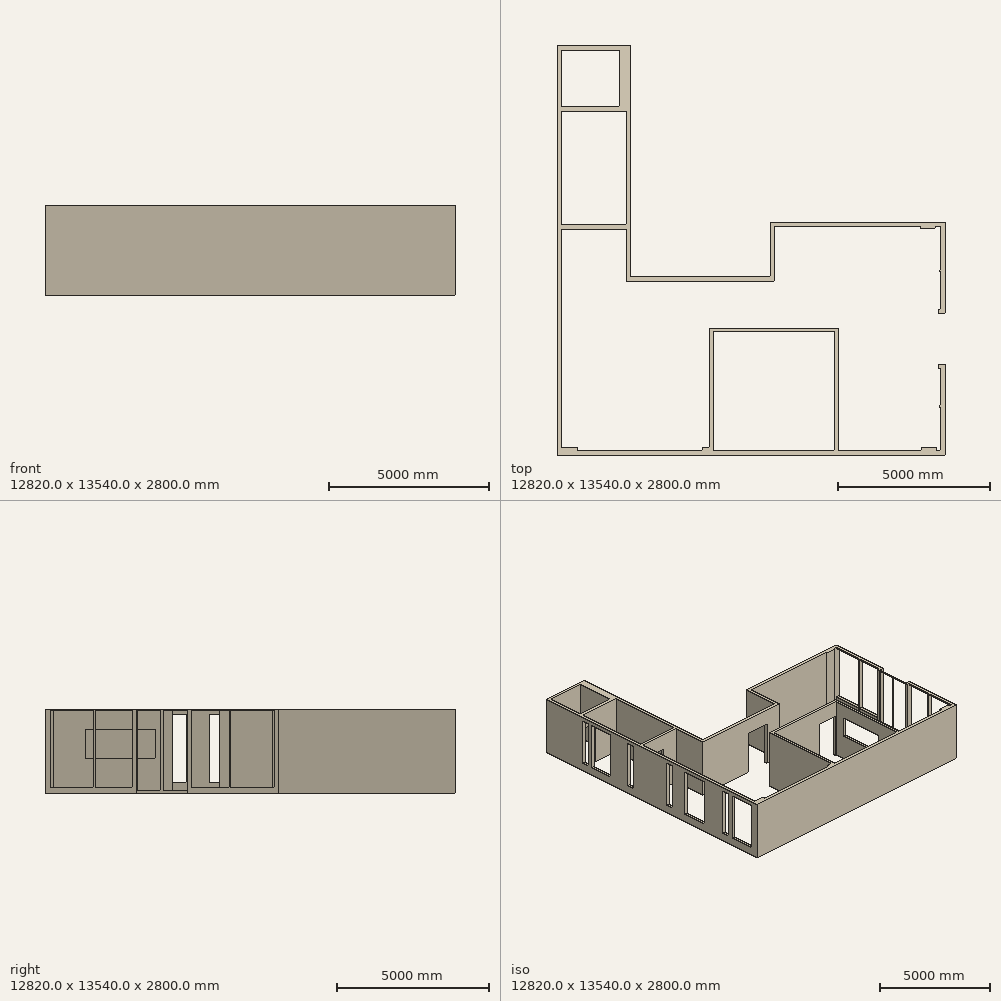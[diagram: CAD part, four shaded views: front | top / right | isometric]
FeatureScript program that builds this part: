
annotation { "Feature Type Name" : "Feature", "Feature Type Description" : "" }
export const myFeature = defineFeature(function(context is Context, id is Id, definition is map)
    precondition{}
    {
        {
            var Q0;
            Q0=qCreatedBy(makeId("Top.planeOp"),FACE);
            var sketch = newSketch(context, id + "F0", { "sketchPlane" : qUnion([Q0])});
            skLineSegment(sketch, "E0", {"start": v(0, 13240) * mm, "end": v(1900, 13240) * mm});
            skLineSegment(sketch, "E1", {"start": v(2130, 11200) * mm, "end": v(2130, 5610) * mm});
            skLineSegment(sketch, "E2", {"start": v(2130, 5610) * mm, "end": v(7030, 5610) * mm});
            skLineSegment(sketch, "E3", {"start": v(7030, 5610) * mm, "end": v(7030, 7400) * mm});
            skLineSegment(sketch, "E4", {"start": v(7030, 7400) * mm, "end": v(11840, 7400) * mm});
            skLineSegment(sketch, "E5", {"start": v(12500, 7400) * mm, "end": v(12500, 5970) * mm});
            skLineSegment(sketch, "E6", {"start": v(12500, 0) * mm, "end": v(12360, 0) * mm});
            skLineSegment(sketch, "E7", {"start": v(0, 125) * mm, "end": v(0, 11200) * mm});
            skLineSegment(sketch, "E8", {"start": v(-150, 13390) * mm, "end": v(-150, -150) * mm});
            skLineSegment(sketch, "E9", {"start": v(-150, -150) * mm, "end": v(12670, -150) * mm});
            skLineSegment(sketch, "E10", {"start": v(12670, -150) * mm, "end": v(12670, 2865) * mm});
            skLineSegment(sketch, "E11", {"start": v(12670, 7550) * mm, "end": v(6880, 7550) * mm});
            skLineSegment(sketch, "E12", {"start": v(2280, 13390) * mm, "end": v(-150, 13390) * mm});
            skLineSegment(sketch, "E13", {"start": v(2130, 11200) * mm, "end": v(0, 11200) * mm});
            skLineSegment(sketch, "E14", {"start": v(0, 11360) * mm, "end": v(1900, 11360) * mm});
            skLineSegment(sketch, "E15", {"start": v(1900, 11360) * mm, "end": v(1900, 13240) * mm});
            skLineSegment(sketch, "E16", {"start": v(0, 125) * mm, "end": v(500, 125) * mm});
            skLineSegment(sketch, "E17", {"start": v(500, 125) * mm, "end": v(500, 0) * mm});
            skLineSegment(sketch, "E18", {"start": v(4630, 0) * mm, "end": v(4630, 110) * mm});
            skLineSegment(sketch, "E19", {"start": v(4630, 110) * mm, "end": v(5010, 110) * mm});
            skLineSegment(sketch, "E20", {"start": v(5010, 110) * mm, "end": v(5010, 0) * mm});
            skLineSegment(sketch, "E21.trimOffspring", {"start": v(4630, 0) * mm, "end": v(500, 0) * mm});
            skLineSegment(sketch, "E22", {"start": v(2280, 5760) * mm, "end": v(2280, 13390) * mm});
            skLineSegment(sketch, "E23", {"start": v(2280, 5760) * mm, "end": v(6880, 5760) * mm});
            skLineSegment(sketch, "E24", {"start": v(6880, 5760) * mm, "end": v(6880, 7550) * mm});
            skLineSegment(sketch, "E25.top", {"start": v(11840, 7350) * mm, "end": v(12340, 7350) * mm});
            skLineSegment(sketch, "E25.left", {"start": v(11840, 7400) * mm, "end": v(11840, 7350) * mm});
            skLineSegment(sketch, "E25.right", {"start": v(12340, 7400) * mm, "end": v(12340, 7350) * mm});
            skLineSegment(sketch, "E26.trimOffspring", {"start": v(12340, 7400) * mm, "end": v(12500, 7400) * mm});
            skLineSegment(sketch, "E27.top", {"start": v(11860, 110) * mm, "end": v(12360, 110) * mm});
            skLineSegment(sketch, "E27.left", {"start": v(11860, 0) * mm, "end": v(11860, 110) * mm});
            skLineSegment(sketch, "E27.right", {"start": v(12360, 0) * mm, "end": v(12360, 110) * mm});
            skLineSegment(sketch, "E28.trimOffspring", {"start": v(11860, 0) * mm, "end": v(5010, 0) * mm});
            skLineSegment(sketch, "E29.trimOffspring", {"start": v(0, 11360) * mm, "end": v(0, 13240) * mm});
            skLineSegment(sketch, "E30", {"start": v(12500, 5970) * mm, "end": v(12470, 5970) * mm});
            skLineSegment(sketch, "E31", {"start": v(12470, 5970) * mm, "end": v(12470, 5910) * mm});
            skLineSegment(sketch, "E32", {"start": v(12470, 5910) * mm, "end": v(12500, 5910) * mm});
            skLineSegment(sketch, "E33.trimOffspring", {"start": v(12500, 5910) * mm, "end": v(12500, 4670) * mm});
            skLineSegment(sketch, "E34", {"start": v(12500, 1430) * mm, "end": v(12470, 1430) * mm});
            skLineSegment(sketch, "E35", {"start": v(12470, 1430) * mm, "end": v(12470, 1490) * mm});
            skLineSegment(sketch, "E36", {"start": v(12470, 1490) * mm, "end": v(12500, 1490) * mm});
            skLineSegment(sketch, "E37.trimOffspring", {"start": v(12500, 1430) * mm, "end": v(12500, 0) * mm});
            skLineSegment(sketch, "E38", {"start": v(12500, 4670) * mm, "end": v(12420, 4670) * mm});
            skLineSegment(sketch, "E39", {"start": v(12420, 4670) * mm, "end": v(12420, 2730) * mm});
            skLineSegment(sketch, "E40", {"start": v(12420, 2730) * mm, "end": v(12500, 2730) * mm});
            skLineSegment(sketch, "E41.trimOffspring", {"start": v(12500, 2730) * mm, "end": v(12500, 1490) * mm});
            skLineSegment(sketch, "E42", {"start": v(12670, 4535) * mm, "end": v(12440, 4535) * mm});
            skLineSegment(sketch, "E43", {"start": v(12440, 4535) * mm, "end": v(12440, 2865) * mm});
            skLineSegment(sketch, "E44", {"start": v(12440, 2865) * mm, "end": v(12670, 2865) * mm});
            skLineSegment(sketch, "E45.trimOffspring", {"start": v(12670, 4535) * mm, "end": v(12670, 7550) * mm});
            skSolve(sketch);
        }
        {
            var Q0;
            Q0 = qSketchRegion(id + "F0", true);
            extrude(context, id + "F1", {"entities" : qUnion([Q0]), "depth" : 2800 * mm, "offsetDistance" : 25 * mm});
        }
        {
            var Q0;
            Q0=makeQuery(id+"F1.opExtrude","SWEPT_FACE",FACE,{"disambiguationData":[OSD([sQuery(id+"F0.wireOp",EDGE,"E13")])]});
            var sketch = newSketch(context, id + "F2", { "sketchPlane" : qUnion([Q0])});
            skLineSegment(sketch, "E46.bottom", {"start": v(70, 0) * mm, "end": v(840, 0) * mm});
            skLineSegment(sketch, "E46.top", {"start": v(70, 2050) * mm, "end": v(840, 2050) * mm});
            skLineSegment(sketch, "E46.left", {"start": v(70, 0) * mm, "end": v(70, 2050) * mm});
            skLineSegment(sketch, "E46.right", {"start": v(840, 0) * mm, "end": v(840, 2050) * mm});
            skSolve(sketch);
        }
        {
            var Q0;
            Q0=makeQuery(id+"F2.imprint","IMPRINT",FACE,{"disambiguationData":[TD([[makeQuery(id+"F2.imprint","IMPRINT",EDGE,{"derivedFrom":sQuery(id+"F2.wireOp",EDGE,"E46.bottom")}),-1.0]])]});
            extrude(context, id + "F3", {"entities" : qUnion([Q0]), "operationType" : NewBodyOperationType.REMOVE, "endBound" : BoundingType.UP_TO_NEXT, "oppositeDirection" : true, "depth" : 25 * mm, "offsetDistance" : 25 * mm});
        }
        {
            var Q0;
            Q0=makeQuery(id+"F1.opExtrude","SWEPT_FACE",FACE,{"disambiguationData":[OSD([sQuery(id+"F0.wireOp",EDGE,"E13")])]});
            cPlane(context, id + "F4", {"entities" : qUnion([Q0]), "cplaneType" : CPlaneType.OFFSET, "offset" : 3730 * mm, "width" : 150 * mm, "height" : 150 * mm});
        }
        {
            var Q0;
            Q0=qCreatedBy(id+"F4.planeOp",FACE);
            var sketch = newSketch(context, id + "F5", { "sketchPlane" : qUnion([Q0])});
            skLineSegment(sketch, "E47.bottom", {"start": v(0, 0) * mm, "end": v(560, 0) * mm});
            skLineSegment(sketch, "E47.top", {"start": v(0, 2800) * mm, "end": v(2130, 2800) * mm});
            skLineSegment(sketch, "E47.left", {"start": v(0, 0) * mm, "end": v(0, 2800) * mm});
            skLineSegment(sketch, "E47.right", {"start": v(2130, 0) * mm, "end": v(2130, 2800) * mm});
            skLineSegment(sketch, "E48.top", {"start": v(560, 2050) * mm, "end": v(1330, 2050) * mm});
            skLineSegment(sketch, "E48.left", {"start": v(560, 0) * mm, "end": v(560, 2050) * mm});
            skLineSegment(sketch, "E48.right", {"start": v(1330, 0) * mm, "end": v(1330, 2050) * mm});
            skLineSegment(sketch, "E49.trimOffspring", {"start": v(1330, 0) * mm, "end": v(2130, 0) * mm});
            skSolve(sketch);
        }
        {
            var Q0;
            Q0=makeQuery(id+"F5.imprint","IMPRINT",FACE,{"disambiguationData":[TD([[makeQuery(id+"F5.imprint","IMPRINT",EDGE,{"derivedFrom":sQuery(id+"F5.wireOp",EDGE,"E47.bottom")}),1.0]])]});
            extrude(context, id + "F6", {"entities" : qUnion([Q0]), "operationType" : NewBodyOperationType.ADD, "depth" : 150 * mm, "offsetDistance" : 25 * mm});
        }
        {
            var Q0;
            Q0=makeQuery(id+"F1.opExtrude","SWEPT_FACE",FACE,{"disambiguationData":[OSD([sQuery(id+"F0.wireOp",EDGE,"E2")])]});
            var sketch = newSketch(context, id + "F7", { "sketchPlane" : qUnion([Q0])});
            skLineSegment(sketch, "E50.bottom", {"start": v(6250, 0) * mm, "end": v(5070, 0) * mm});
            skLineSegment(sketch, "E50.top", {"start": v(6250, 2050) * mm, "end": v(5070, 2050) * mm});
            skLineSegment(sketch, "E50.left", {"start": v(6250, 0) * mm, "end": v(6250, 2050) * mm});
            skLineSegment(sketch, "E50.right", {"start": v(5070, 0) * mm, "end": v(5070, 2050) * mm});
            skSolve(sketch);
        }
        {
            var Q0;
            Q0=makeQuery(id+"F7.imprint","IMPRINT",FACE,{"disambiguationData":[TD([[makeQuery(id+"F7.imprint","IMPRINT",EDGE,{"derivedFrom":sQuery(id+"F7.wireOp",EDGE,"E50.bottom")}),1.0]])]});
            extrude(context, id + "F8", {"entities" : qUnion([Q0]), "operationType" : NewBodyOperationType.REMOVE, "endBound" : BoundingType.UP_TO_NEXT, "oppositeDirection" : true, "depth" : 25 * mm, "offsetDistance" : 25 * mm});
        }
        {
            var Q0;
            Q0=makeQuery(id+"F1.opExtrude","SWEPT_FACE",FACE,{"disambiguationData":[OSD([sQuery(id+"F0.wireOp",EDGE,"E8")])]});
            var sketch = newSketch(context, id + "F9", { "sketchPlane" : qUnion([Q0])});
            skLineSegment(sketch, "E51.bottom", {"start": v(-240, 390) * mm, "end": v(-1460, 390) * mm});
            skLineSegment(sketch, "E51.top", {"start": v(-240, 2610) * mm, "end": v(-1460, 2610) * mm});
            skLineSegment(sketch, "E51.left", {"start": v(-240, 390) * mm, "end": v(-240, 2610) * mm});
            skLineSegment(sketch, "E51.right", {"start": v(-1460, 390) * mm, "end": v(-1460, 2610) * mm});
            skLineSegment(sketch, "E52.bottom", {"start": v(-1660, 2610) * mm, "end": v(-2050, 2610) * mm});
            skLineSegment(sketch, "E52.top", {"start": v(-1660, 390) * mm, "end": v(-2050, 390) * mm});
            skLineSegment(sketch, "E52.left", {"start": v(-1660, 2610) * mm, "end": v(-1660, 390) * mm});
            skLineSegment(sketch, "E52.right", {"start": v(-2050, 2610) * mm, "end": v(-2050, 390) * mm});
            skLineSegment(sketch, "E53.bottom", {"start": v(-3240, 390) * mm, "end": v(-4500, 390) * mm});
            skLineSegment(sketch, "E53.top", {"start": v(-3240, 2610) * mm, "end": v(-4500, 2610) * mm});
            skLineSegment(sketch, "E53.left", {"start": v(-3240, 390) * mm, "end": v(-3240, 2610) * mm});
            skLineSegment(sketch, "E53.right", {"start": v(-4500, 390) * mm, "end": v(-4500, 2610) * mm});
            skLineSegment(sketch, "E54.bottom", {"start": v(-5270, 2610) * mm, "end": v(-5660, 2610) * mm});
            skLineSegment(sketch, "E54.top", {"start": v(-5270, 390) * mm, "end": v(-5660, 390) * mm});
            skLineSegment(sketch, "E54.left", {"start": v(-5270, 2610) * mm, "end": v(-5270, 390) * mm});
            skLineSegment(sketch, "E54.right", {"start": v(-5660, 2610) * mm, "end": v(-5660, 390) * mm});
            skLineSegment(sketch, "E55.bottom", {"start": v(-7780, 390) * mm, "end": v(-8170, 390) * mm});
            skLineSegment(sketch, "E55.top", {"start": v(-7780, 2610) * mm, "end": v(-8170, 2610) * mm});
            skLineSegment(sketch, "E55.left", {"start": v(-7780, 390) * mm, "end": v(-7780, 2610) * mm});
            skLineSegment(sketch, "E55.right", {"start": v(-8170, 390) * mm, "end": v(-8170, 2610) * mm});
            skLineSegment(sketch, "E56.bottom", {"start": v(-9250, 2610) * mm, "end": v(-10470, 2610) * mm});
            skLineSegment(sketch, "E56.top", {"start": v(-9250, 390) * mm, "end": v(-10470, 390) * mm});
            skLineSegment(sketch, "E56.left", {"start": v(-9250, 2610) * mm, "end": v(-9250, 390) * mm});
            skLineSegment(sketch, "E56.right", {"start": v(-10470, 2610) * mm, "end": v(-10470, 390) * mm});
            skLineSegment(sketch, "E57.bottom", {"start": v(-10670, 390) * mm, "end": v(-11060, 390) * mm});
            skLineSegment(sketch, "E57.top", {"start": v(-10670, 2610) * mm, "end": v(-11060, 2610) * mm});
            skLineSegment(sketch, "E57.left", {"start": v(-10670, 390) * mm, "end": v(-10670, 2610) * mm});
            skLineSegment(sketch, "E57.right", {"start": v(-11060, 390) * mm, "end": v(-11060, 2610) * mm});
            skSolve(sketch);
        }
        {
            var Q0;
            Q0=makeQuery(id+"F9.imprint","IMPRINT",FACE,{"disambiguationData":[TD([[makeQuery(id+"F9.imprint","IMPRINT",EDGE,{"derivedFrom":sQuery(id+"F9.wireOp",EDGE,"E54.bottom")}),1.0]])]});
            var Q1;
            Q1=makeQuery(id+"F9.imprint","IMPRINT",FACE,{"disambiguationData":[TD([[makeQuery(id+"F9.imprint","IMPRINT",EDGE,{"derivedFrom":sQuery(id+"F9.wireOp",EDGE,"E53.bottom")}),-1.0]])]});
            var Q2;
            Q2=makeQuery(id+"F9.imprint","IMPRINT",FACE,{"disambiguationData":[TD([[makeQuery(id+"F9.imprint","IMPRINT",EDGE,{"derivedFrom":sQuery(id+"F9.wireOp",EDGE,"E52.bottom")}),1.0]])]});
            var Q3;
            Q3=makeQuery(id+"F9.imprint","IMPRINT",FACE,{"disambiguationData":[TD([[makeQuery(id+"F9.imprint","IMPRINT",EDGE,{"derivedFrom":sQuery(id+"F9.wireOp",EDGE,"E51.bottom")}),-1.0]])]});
            var Q4;
            Q4=makeQuery(id+"F9.imprint","IMPRINT",FACE,{"disambiguationData":[TD([[makeQuery(id+"F9.imprint","IMPRINT",EDGE,{"derivedFrom":sQuery(id+"F9.wireOp",EDGE,"E55.bottom")}),-1.0]])]});
            var Q5;
            Q5=makeQuery(id+"F9.imprint","IMPRINT",FACE,{"disambiguationData":[TD([[makeQuery(id+"F9.imprint","IMPRINT",EDGE,{"derivedFrom":sQuery(id+"F9.wireOp",EDGE,"E56.bottom")}),1.0]])]});
            var Q6;
            Q6=makeQuery(id+"F9.imprint","IMPRINT",FACE,{"disambiguationData":[TD([[makeQuery(id+"F9.imprint","IMPRINT",EDGE,{"derivedFrom":sQuery(id+"F9.wireOp",EDGE,"E57.bottom")}),-1.0]])]});
            extrude(context, id + "F10", {"entities" : qUnion([Q0, Q1, Q2, Q3, Q4, Q5, Q6]), "operationType" : NewBodyOperationType.REMOVE, "endBound" : BoundingType.UP_TO_NEXT, "oppositeDirection" : true, "depth" : 25 * mm, "offsetDistance" : 25 * mm});
        }
        {
            var Q0;
            Q0=makeQuery(id+"F1.opExtrude","SWEPT_FACE",FACE,{"disambiguationData":[OSD([sQuery(id+"F0.wireOp",EDGE,"E10")])]});
            var sketch = newSketch(context, id + "F11", { "sketchPlane" : qUnion([Q0])});
            skLineSegment(sketch, "E58.bottom", {"start": v(2730, 200) * mm, "end": v(1490, 200) * mm});
            skLineSegment(sketch, "E58.top", {"start": v(2730, 2760) * mm, "end": v(1490, 2760) * mm});
            skLineSegment(sketch, "E58.left", {"start": v(2730, 200) * mm, "end": v(2730, 2760) * mm});
            skLineSegment(sketch, "E58.right", {"start": v(1490, 200) * mm, "end": v(1490, 2760) * mm});
            skLineSegment(sketch, "E59.bottom", {"start": v(1430, 200) * mm, "end": v(0, 200) * mm});
            skLineSegment(sketch, "E59.top", {"start": v(1430, 2760) * mm, "end": v(0, 2760) * mm});
            skLineSegment(sketch, "E59.left", {"start": v(1430, 200) * mm, "end": v(1430, 2760) * mm});
            skLineSegment(sketch, "E59.right", {"start": v(0, 200) * mm, "end": v(0, 2760) * mm});
            skLineSegment(sketch, "E60.bottom", {"start": v(4670, 200) * mm, "end": v(5910, 200) * mm});
            skLineSegment(sketch, "E60.top", {"start": v(4670, 2760) * mm, "end": v(5910, 2760) * mm});
            skLineSegment(sketch, "E60.left", {"start": v(4670, 200) * mm, "end": v(4670, 2760) * mm});
            skLineSegment(sketch, "E60.right", {"start": v(5910, 200) * mm, "end": v(5910, 2760) * mm});
            skLineSegment(sketch, "E61.bottom", {"start": v(5970, 200) * mm, "end": v(7400, 200) * mm});
            skLineSegment(sketch, "E61.top", {"start": v(5970, 2760) * mm, "end": v(7400, 2760) * mm});
            skLineSegment(sketch, "E61.left", {"start": v(5970, 200) * mm, "end": v(5970, 2760) * mm});
            skLineSegment(sketch, "E61.right", {"start": v(7400, 200) * mm, "end": v(7400, 2760) * mm});
            skLineSegment(sketch, "E62.bottom", {"start": v(4525, 110) * mm, "end": v(3740, 110) * mm});
            skLineSegment(sketch, "E62.top", {"start": v(4525, 2760) * mm, "end": v(3740, 2760) * mm});
            skLineSegment(sketch, "E62.left", {"start": v(4525, 110) * mm, "end": v(4525, 2760) * mm});
            skLineSegment(sketch, "E62.right", {"start": v(3740, 110) * mm, "end": v(3740, 2760) * mm});
            skLineSegment(sketch, "E63.bottom", {"start": v(3660, 2760) * mm, "end": v(2875, 2760) * mm});
            skLineSegment(sketch, "E63.top", {"start": v(3660, 110) * mm, "end": v(2875, 110) * mm});
            skLineSegment(sketch, "E63.left", {"start": v(3660, 2760) * mm, "end": v(3660, 110) * mm});
            skLineSegment(sketch, "E63.right", {"start": v(2875, 2760) * mm, "end": v(2875, 110) * mm});
            skSolve(sketch);
        }
        {
            var Q0;
            Q0=makeQuery(id+"F11.imprint","IMPRINT",FACE,{"disambiguationData":[TD([[makeQuery(id+"F11.imprint","IMPRINT",EDGE,{"derivedFrom":sQuery(id+"F11.wireOp",EDGE,"E59.bottom")}),-1.0]])]});
            var Q1;
            Q1=makeQuery(id+"F11.imprint","IMPRINT",FACE,{"disambiguationData":[TD([[makeQuery(id+"F11.imprint","IMPRINT",EDGE,{"derivedFrom":sQuery(id+"F11.wireOp",EDGE,"E58.bottom")}),-1.0]])]});
            var Q2;
            Q2=makeQuery(id+"F11.imprint","IMPRINT",FACE,{"disambiguationData":[TD([[makeQuery(id+"F11.imprint","IMPRINT",EDGE,{"derivedFrom":sQuery(id+"F11.wireOp",EDGE,"E63.bottom")}),1.0]])]});
            var Q3;
            Q3=makeQuery(id+"F11.imprint","IMPRINT",FACE,{"disambiguationData":[TD([[makeQuery(id+"F11.imprint","IMPRINT",EDGE,{"derivedFrom":sQuery(id+"F11.wireOp",EDGE,"E62.bottom")}),-1.0]])]});
            var Q4;
            Q4=makeQuery(id+"F11.imprint","IMPRINT",FACE,{"disambiguationData":[TD([[makeQuery(id+"F11.imprint","IMPRINT",EDGE,{"derivedFrom":sQuery(id+"F11.wireOp",EDGE,"E60.bottom")}),1.0]])]});
            var Q5;
            Q5=makeQuery(id+"F11.imprint","IMPRINT",FACE,{"disambiguationData":[TD([[makeQuery(id+"F11.imprint","IMPRINT",EDGE,{"derivedFrom":sQuery(id+"F11.wireOp",EDGE,"E61.bottom")}),1.0]])]});
            var Q6;
            Q6=makeQuery(id+"F1.opExtrude","SWEPT_FACE",FACE,{"disambiguationData":[OSD([sQuery(id+"F0.wireOp",EDGE,"E39")])]});
            extrude(context, id + "F12", {"entities" : qUnion([Q0, Q1, Q2, Q3, Q4, Q5]), "operationType" : NewBodyOperationType.REMOVE, "endBound" : BoundingType.UP_TO_SURFACE, "oppositeDirection" : true, "depth" : 25 * mm, "endBoundEntityFace" : qUnion([Q6]), "offsetDistance" : 25 * mm});
        }
        {
            var Q0;
            Q0=qCreatedBy(makeId("Top.planeOp"),FACE);
            var sketch = newSketch(context, id + "F13", { "sketchPlane" : qUnion([Q0])});
            skLineSegment(sketch, "E64", {"start": v(4880, 0) * mm, "end": v(4880, 4060) * mm});
            skLineSegment(sketch, "E65", {"start": v(4880, 4060) * mm, "end": v(9140, 4060) * mm});
            skLineSegment(sketch, "E66", {"start": v(9140, 4060) * mm, "end": v(9140, 0) * mm});
            skLineSegment(sketch, "E67", {"start": v(9140, 0) * mm, "end": v(9010, 0) * mm});
            skLineSegment(sketch, "E68", {"start": v(9010, 0) * mm, "end": v(9010, 3930) * mm});
            skLineSegment(sketch, "E69", {"start": v(5010, 3930) * mm, "end": v(5010, 0) * mm});
            skLineSegment(sketch, "E70", {"start": v(5010, 0) * mm, "end": v(4880, 0) * mm});
            skLineSegment(sketch, "E71.trimOffspring", {"start": v(9010, 3930) * mm, "end": v(5010, 3930) * mm});
            skSolve(sketch);
        }
        {
            var Q0;
            Q0 = qSketchRegion(id + "F13", true);
            extrude(context, id + "F14", {"entities" : qUnion([Q0]), "operationType" : NewBodyOperationType.ADD, "depth" : 2800 * mm, "offsetDistance" : 25 * mm});
        }
        {
            var Q0;
            Q0=makeQuery(id+"F14.opExtrude","SWEPT_FACE",FACE,{"disambiguationData":[OSD([sQuery(id+"F13.wireOp",EDGE,"E71.trimOffspring")])]});
            var sketch = newSketch(context, id + "F15", { "sketchPlane" : qUnion([Q0])});
            skLineSegment(sketch, "E72.bottom", {"start": v(8950, 0) * mm, "end": v(7960, 0) * mm});
            skLineSegment(sketch, "E72.top", {"start": v(8950, 2050) * mm, "end": v(7960, 2050) * mm});
            skLineSegment(sketch, "E72.left", {"start": v(8950, 0) * mm, "end": v(8950, 2050) * mm});
            skLineSegment(sketch, "E72.right", {"start": v(7960, 0) * mm, "end": v(7960, 2050) * mm});
            skSolve(sketch);
        }
        {
            var Q0;
            Q0=makeQuery(id+"F15.imprint","IMPRINT",FACE,{"disambiguationData":[TD([[makeQuery(id+"F15.imprint","IMPRINT",EDGE,{"derivedFrom":sQuery(id+"F15.wireOp",EDGE,"E72.bottom")}),-1.0]])]});
            extrude(context, id + "F16", {"entities" : qUnion([Q0]), "operationType" : NewBodyOperationType.REMOVE, "endBound" : BoundingType.UP_TO_NEXT, "oppositeDirection" : true, "depth" : 25 * mm, "offsetDistance" : 25 * mm});
        }
        {
            var Q0;
            Q0=makeQuery(id+"F14.opExtrude","SWEPT_FACE",FACE,{"disambiguationData":[OSD([sQuery(id+"F13.wireOp",EDGE,"E66")])]});
            var sketch = newSketch(context, id + "F17", { "sketchPlane" : qUnion([Q0])});
            skLineSegment(sketch, "E73.bottom", {"start": v(1180, 1180) * mm, "end": v(3470, 1180) * mm});
            skLineSegment(sketch, "E73.top", {"start": v(1180, 2140) * mm, "end": v(3470, 2140) * mm});
            skLineSegment(sketch, "E73.left", {"start": v(1180, 1180) * mm, "end": v(1180, 2140) * mm});
            skLineSegment(sketch, "E73.right", {"start": v(3470, 1180) * mm, "end": v(3470, 2140) * mm});
            skSolve(sketch);
        }
        {
            var Q0;
            Q0=makeQuery(id+"F17.imprint","IMPRINT",FACE,{"disambiguationData":[TD([[makeQuery(id+"F17.imprint","IMPRINT",EDGE,{"derivedFrom":sQuery(id+"F17.wireOp",EDGE,"E73.bottom")}),1.0]])]});
            extrude(context, id + "F18", {"entities" : qUnion([Q0]), "operationType" : NewBodyOperationType.REMOVE, "endBound" : BoundingType.UP_TO_NEXT, "oppositeDirection" : true, "depth" : 25 * mm, "offsetDistance" : 25 * mm});
        }
    });
